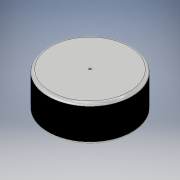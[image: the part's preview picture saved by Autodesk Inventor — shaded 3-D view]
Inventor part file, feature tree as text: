
AUTODESK INVENTOR PART (.ipt)
format: ipt  version: 2019 (Build 230136000, 136)  size: 121,856 bytes
history: native  units: in
note: dims shown in document units (in); Inventor stores cm internally (conversion verified against a paired STEP export)
features: other x3, sketch x1
ambient origin geometry x8: Origin, YZ Plane, XZ Plane, XY Plane, X Axis, Y Axis, Z Axis, Center Point
bodies: Solid1 (feature_tree)
feature tree (4):
  other  "carromwheel.ipt"
  other  "Solid1::carromwheel.ipt"
  other  "TaggingFeature1"
  sketch  "Sketch3"  dims[d0=0.1969in]
